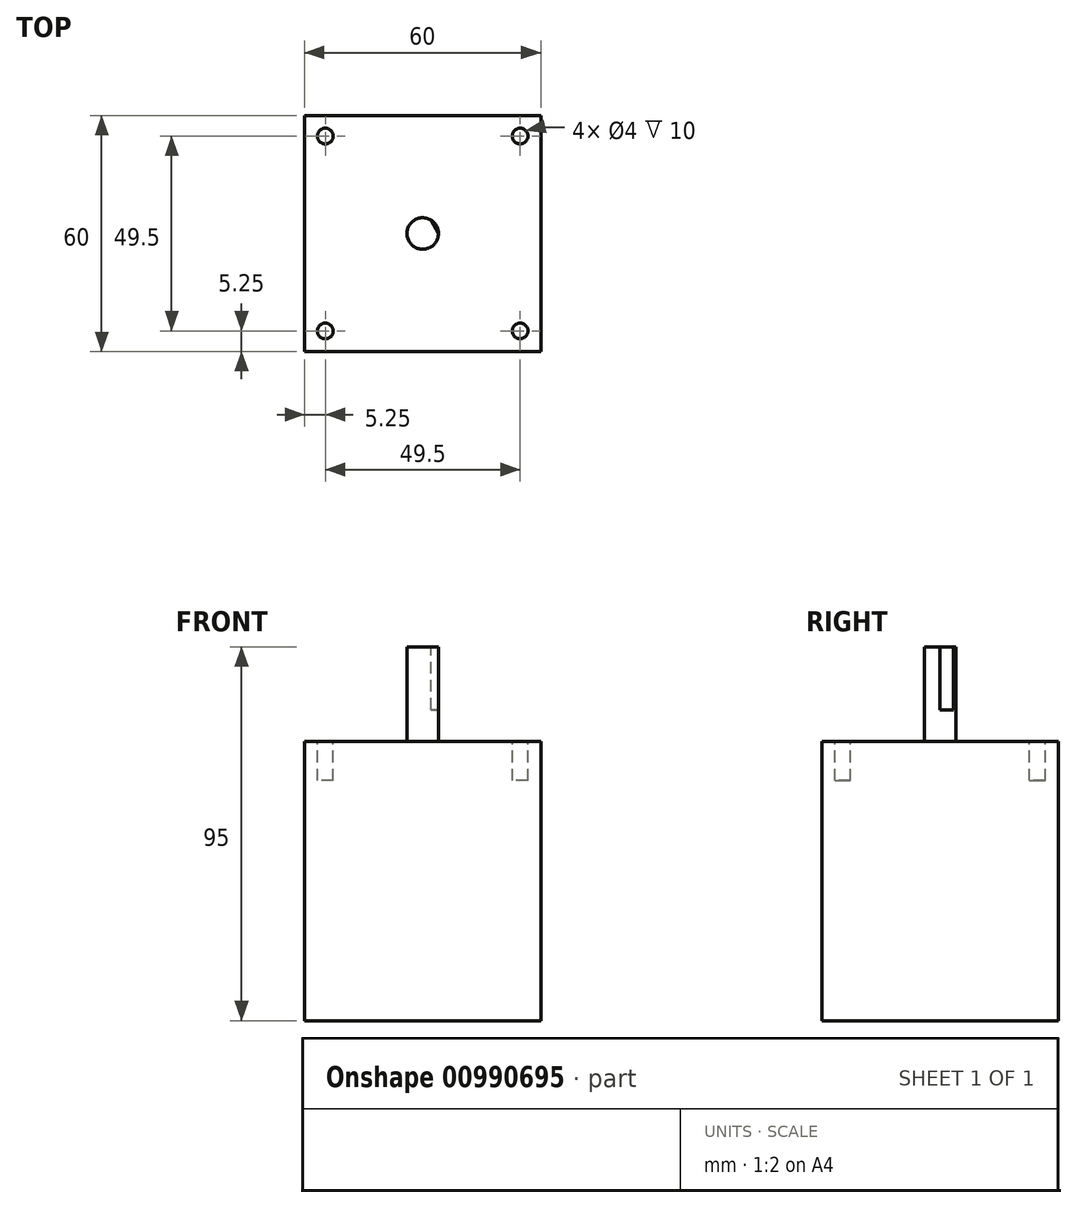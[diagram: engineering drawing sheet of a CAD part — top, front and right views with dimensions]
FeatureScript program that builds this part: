
annotation { "Feature Type Name" : "Feature", "Feature Type Description" : "" }
export const myFeature = defineFeature(function(context is Context, id is Id, definition is map)
    precondition{}
    {
        {
            var Q0;
            Q0=qCreatedBy(makeId("Top.planeOp"),FACE);
            var sketch = newSketch(context, id + "F0", { "sketchPlane" : qUnion([Q0])});
            skLineSegment(sketch, "E0.bottom", {"start": v(30, -30) * mm, "end": v(-30, -30) * mm});
            skLineSegment(sketch, "E0.top", {"start": v(30, 30) * mm, "end": v(-30, 30) * mm});
            skLineSegment(sketch, "E0.left", {"start": v(30, -30) * mm, "end": v(30, 30) * mm});
            skLineSegment(sketch, "E0.right", {"start": v(-30, -30) * mm, "end": v(-30, 30) * mm});
            skPoint(sketch, "E0.middle", {"position": v(0, 0) * mm});
            skSolve(sketch);
        }
        {
            var Q0;
            Q0 = qSketchRegion(id + "F0", true);
            extrude(context, id + "F1", {"entities" : qUnion([Q0]), "depth" : 71 * mm, "offsetDistance" : 25 * mm});
        }
        {
            var Q0;
            Q0=makeQuery(id+"F1.opExtrude","CAP_FACE",FACE,{"disambiguationData":[OSD([sQuery(id+"F0.wireOp",EDGE,"E0.bottom"),sQuery(id+"F0.wireOp",EDGE,"E0.top"),sQuery(id+"F0.wireOp",EDGE,"E0.left"),sQuery(id+"F0.wireOp",EDGE,"E0.right")])],"isStart":false});
            var sketch = newSketch(context, id + "F2", { "sketchPlane" : qUnion([Q0])});
            skLineSegment(sketch, "E1.bottom", {"start": v(24.75, -24.75) * mm, "end": v(-24.75, -24.75) * mm, "construction": true});
            skLineSegment(sketch, "E1.top", {"start": v(24.75, 24.75) * mm, "end": v(-24.75, 24.75) * mm, "construction": true});
            skLineSegment(sketch, "E1.left", {"start": v(24.75, -24.75) * mm, "end": v(24.75, 24.75) * mm, "construction": true});
            skLineSegment(sketch, "E1.right", {"start": v(-24.75, -24.75) * mm, "end": v(-24.75, 24.75) * mm, "construction": true});
            skPoint(sketch, "E1.middle", {"position": v(0, 0) * mm});
            skCircle(sketch, "E2", {"center": v(-24.75, -24.75) * mm, "radius": 2 * mm});
            skCircle(sketch, "E3.MirrorC", {"center": v(24.75, -24.75) * mm, "radius": 2 * mm});
            skCircle(sketch, "E4.MirrorC", {"center": v(-24.75, 24.75) * mm, "radius": 2 * mm});
            skCircle(sketch, "E5.MirrorC", {"center": v(24.75, 24.75) * mm, "radius": 2 * mm});
            skSolve(sketch);
        }
        {
            var Q0;
            Q0 = qSketchRegion(id + "F2", true);
            extrude(context, id + "F3", {"entities" : qUnion([Q0]), "operationType" : NewBodyOperationType.REMOVE, "oppositeDirection" : true, "depth" : 10 * mm, "offsetDistance" : 25 * mm});
        }
        {
            var Q0;
            Q0=makeQuery(id+"F2.imprint","IMPRINT",FACE,{"disambiguationData":[TD([[makeQuery(id+"F2.imprint","IMPRINT",EDGE,{"derivedFrom":sQuery(id+"F2.wireOp",EDGE,"E2")}),-1.0]])]});
            var sketch = newSketch(context, id + "F4", { "sketchPlane" : qUnion([Q0])});
            skCircle(sketch, "E6", {"center": v(0, 0) * mm, "radius": 4 * mm});
            skSolve(sketch);
        }
        {
            var Q0;
            Q0 = qSketchRegion(id + "F4", true);
            extrude(context, id + "F5", {"entities" : qUnion([Q0]), "depth" : 24 * mm, "offsetDistance" : 25 * mm});
        }
        {
            var Q0;
            Q0=makeQuery(id+"F5.opExtrude","CAP_FACE",FACE,{"disambiguationData":[OSD([sQuery(id+"F4.wireOp",EDGE,"E6")])],"isStart":false});
            var sketch = newSketch(context, id + "F6", { "sketchPlane" : qUnion([Q0])});
            skArc(sketch, "E7", {"start": v(4, 0) * mm, "mid": v(3.5, 1.94) * mm, "end": v(2.13, 3.39) * mm});
            skLineSegment(sketch, "E8", {"start": v(2.13, 3.39) * mm, "end": v(4, 0) * mm});
            skSolve(sketch);
        }
        {
            var Q0;
            Q0 = qSketchRegion(id + "F6", true);
            extrude(context, id + "F7", {"entities" : qUnion([Q0]), "operationType" : NewBodyOperationType.REMOVE, "oppositeDirection" : true, "depth" : 16 * mm, "offsetDistance" : 25 * mm});
        }
    });
